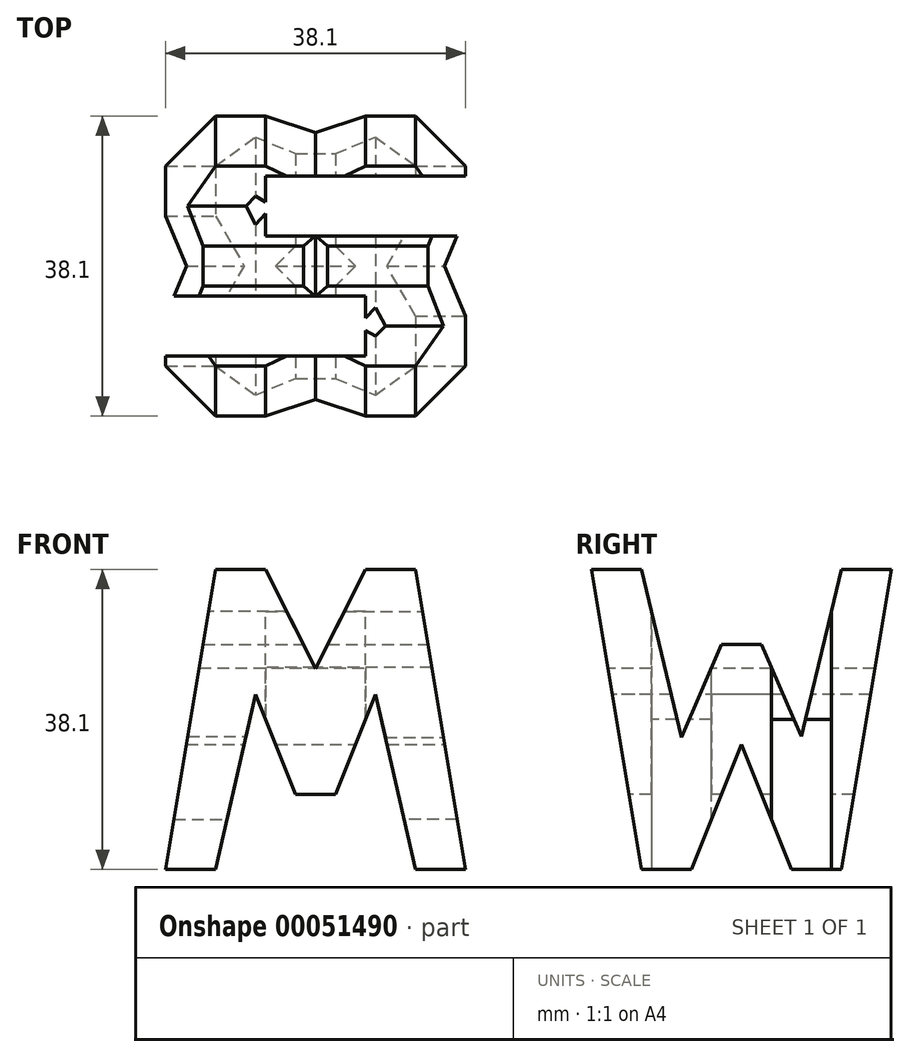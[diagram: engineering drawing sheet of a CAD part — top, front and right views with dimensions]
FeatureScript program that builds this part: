
annotation { "Feature Type Name" : "Feature", "Feature Type Description" : "" }
export const myFeature = defineFeature(function(context is Context, id is Id, definition is map)
    precondition{}
    {
        {
            var Q0;
            Q0=qCreatedBy(makeId("Front.planeOp"),FACE);
            var sketch = newSketch(context, id + "F0", { "sketchPlane" : qUnion([Q0])});
            skLineSegment(sketch, "E0", {"start": v(0, 38.1) * mm, "end": v(0, 0) * mm});
            skLineSegment(sketch, "E1", {"start": v(0, 0) * mm, "end": v(38.1, 0) * mm});
            skLineSegment(sketch, "E2", {"start": v(38.1, 0) * mm, "end": v(38.1, 38.1) * mm});
            skLineSegment(sketch, "E3", {"start": v(38.1, 38.1) * mm, "end": v(0, 38.1) * mm});
            skSolve(sketch);
        }
        {
            var Q0;
            Q0=makeQuery(id+"F0.imprint","IMPRINT",FACE,{"disambiguationData":[TD([[makeQuery(id+"F0.imprint","IMPRINT",EDGE,{"derivedFrom":sQuery(id+"F0.wireOp",EDGE,"E0")}),1.0]])]});
            extrude(context, id + "F1", {"entities" : qUnion([Q0]), "depth" : 38.1 * mm});
        }
        {
            var Q0;
            Q0=qCreatedBy(makeId("Front.planeOp"),FACE);
            cPlane(context, id + "F2", {"entities" : qUnion([Q0]), "cplaneType" : CPlaneType.OFFSET, "offset" : 38.1 * mm, "width" : 152.4 * mm, "height" : 152.4 * mm});
        }
        {
            var Q0;
            Q0=qCreatedBy(makeId("Top.planeOp"),FACE);
            cPlane(context, id + "F3", {"entities" : qUnion([Q0]), "cplaneType" : CPlaneType.OFFSET, "offset" : 38.1 * mm, "width" : 152.4 * mm, "height" : 152.4 * mm});
        }
        {
            var Q0;
            Q0=makeQuery(id+"F1.opExtrude","SWEPT_FACE",FACE,{"disambiguationData":[OSD([sQuery(id+"F0.wireOp",EDGE,"E2")])]});
            var sketch = newSketch(context, id + "F4", { "sketchPlane" : qUnion([Q0])});
            skLineSegment(sketch, "E4", {"start": v(-38.1, 38.1) * mm, "end": v(-31.75, 0) * mm});
            skLineSegment(sketch, "E5", {"start": v(-25.4, 0) * mm, "end": v(-19.05, 15.87) * mm});
            skLineSegment(sketch, "E6", {"start": v(-19.05, 15.87) * mm, "end": v(-12.7, 0) * mm});
            skLineSegment(sketch, "E7", {"start": v(0, 38.1) * mm, "end": v(-6.35, 0) * mm});
            skLineSegment(sketch, "E8", {"start": v(-31.75, 38.1) * mm, "end": v(-26.67, 16.76) * mm});
            skLineSegment(sketch, "E9", {"start": v(-26.67, 16.76) * mm, "end": v(-21.59, 28.57) * mm});
            skLineSegment(sketch, "E10", {"start": v(-21.59, 28.57) * mm, "end": v(-16.5, 28.57) * mm});
            skLineSegment(sketch, "E11", {"start": v(-16.5, 28.57) * mm, "end": v(-11.43, 16.89) * mm});
            skLineSegment(sketch, "E12", {"start": v(-11.43, 16.89) * mm, "end": v(-6.35, 38.1) * mm});
            skSolve(sketch);
        }
        {
            var Q0;
            {var subQ0=sQuery(id+"F4.wireOp",EDGE,"E8");Q0=makeQuery(id+"F4.imprint","IMPRINT",FACE,{"disambiguationData":[TD([[makeQuery(id+"F4.imprint","IMPRINT",EDGE,{"derivedFrom":subQ0}),1.0]])]});}
            var Q1;
            {var subQ0=sQuery(id+"F4.wireOp",EDGE,"E4");Q1=makeQuery(id+"F4.imprint","IMPRINT",FACE,{"disambiguationData":[TD([[makeQuery(id+"F4.imprint","IMPRINT",EDGE,{"derivedFrom":subQ0}),-1.0]])]});}
            var Q2;
            {var subQ0=sQuery(id+"F4.wireOp",EDGE,"E5");Q2=makeQuery(id+"F4.imprint","IMPRINT",FACE,{"disambiguationData":[TD([[makeQuery(id+"F4.imprint","IMPRINT",EDGE,{"derivedFrom":subQ0}),-1.0]])]});}
            var Q3;
            {var subQ0=sQuery(id+"F4.wireOp",EDGE,"E7");Q3=makeQuery(id+"F4.imprint","IMPRINT",FACE,{"disambiguationData":[TD([[makeQuery(id+"F4.imprint","IMPRINT",EDGE,{"derivedFrom":subQ0}),1.0]])]});}
            extrude(context, id + "F5", {"entities" : qUnion([Q0, Q1, Q2, Q3]), "operationType" : NewBodyOperationType.REMOVE, "oppositeDirection" : true, "depth" : 38.1 * mm});
        }
        {
            var Q0;
            Q0=qCreatedBy(id+"F2.planeOp",FACE);
            var sketch = newSketch(context, id + "F6", { "sketchPlane" : qUnion([Q0])});
            skLineSegment(sketch, "E13", {"start": v(0, 0) * mm, "end": v(0, 38.1) * mm});
            skLineSegment(sketch, "E14", {"start": v(0, 38.1) * mm, "end": v(38.1, 38.1) * mm});
            skLineSegment(sketch, "E15", {"start": v(38.1, 38.1) * mm, "end": v(38.1, 0) * mm});
            skLineSegment(sketch, "E16", {"start": v(38.1, 0) * mm, "end": v(0, 0) * mm});
            skLineSegment(sketch, "E17", {"start": v(0, 0) * mm, "end": v(6.35, 38.1) * mm});
            skLineSegment(sketch, "E18", {"start": v(38.1, 0) * mm, "end": v(31.75, 38.1) * mm});
            skLineSegment(sketch, "E19", {"start": v(12.7, 38.1) * mm, "end": v(19.05, 25.51) * mm});
            skLineSegment(sketch, "E20", {"start": v(19.05, 25.51) * mm, "end": v(25.4, 38.1) * mm});
            skLineSegment(sketch, "E21", {"start": v(6.35, 0) * mm, "end": v(11.43, 22.23) * mm});
            skLineSegment(sketch, "E22", {"start": v(11.43, 22.23) * mm, "end": v(16.51, 9.52) * mm});
            skLineSegment(sketch, "E23", {"start": v(16.51, 9.53) * mm, "end": v(21.59, 9.52) * mm});
            skLineSegment(sketch, "E24", {"start": v(21.59, 9.52) * mm, "end": v(26.67, 22.23) * mm});
            skLineSegment(sketch, "E25", {"start": v(26.67, 22.23) * mm, "end": v(31.75, 0) * mm});
            skSolve(sketch);
        }
        {
            var Q0;
            {var subQ0=sQuery(id+"F6.wireOp",EDGE,"E13");Q0=makeQuery(id+"F6.imprint","IMPRINT",FACE,{"disambiguationData":[TD([[makeQuery(id+"F6.imprint","IMPRINT",EDGE,{"derivedFrom":subQ0}),-1.0]])]});}
            var Q1;
            {var subQ0=sQuery(id+"F6.wireOp",EDGE,"E19");Q1=makeQuery(id+"F6.imprint","IMPRINT",FACE,{"disambiguationData":[TD([[makeQuery(id+"F6.imprint","IMPRINT",EDGE,{"derivedFrom":subQ0}),1.0]])]});}
            var Q2;
            {var subQ1=sQuery(id+"F6.wireOp",EDGE,"E21");Q2=makeQuery(id+"F6.imprint","IMPRINT",FACE,{"disambiguationData":[TD([[makeQuery(id+"F6.imprint","IMPRINT",EDGE,{"derivedFrom":subQ1}),-1.0]])]});}
            var Q3;
            {var subQ0=sQuery(id+"F6.wireOp",EDGE,"E15");Q3=makeQuery(id+"F6.imprint","IMPRINT",FACE,{"disambiguationData":[TD([[makeQuery(id+"F6.imprint","IMPRINT",EDGE,{"derivedFrom":subQ0}),-1.0]])]});}
            extrude(context, id + "F7", {"entities" : qUnion([Q0, Q1, Q2, Q3]), "operationType" : NewBodyOperationType.REMOVE, "oppositeDirection" : true, "depth" : 38.1 * mm});
        }
        {
            var Q0;
            Q0=qCreatedBy(id+"F3.planeOp",FACE);
            var sketch = newSketch(context, id + "F8", { "sketchPlane" : qUnion([Q0])});
            skLineSegment(sketch, "E26", {"start": v(38.1, 0) * mm, "end": v(38.1, -38.1) * mm});
            skLineSegment(sketch, "E27", {"start": v(38.1, -38.1) * mm, "end": v(0, -38.1) * mm});
            skLineSegment(sketch, "E28", {"start": v(0, -38.1) * mm, "end": v(0, 0) * mm});
            skLineSegment(sketch, "E29", {"start": v(0, 0) * mm, "end": v(38.1, 0) * mm});
            skLineSegment(sketch, "E30", {"start": v(38.1, -7.62) * mm, "end": v(12.7, -7.62) * mm});
            skLineSegment(sketch, "E31", {"start": v(12.7, -7.62) * mm, "end": v(12.7, -15.24) * mm});
            skLineSegment(sketch, "E32", {"start": v(12.7, -15.24) * mm, "end": v(38.1, -15.24) * mm});
            skLineSegment(sketch, "E33", {"start": v(0, -30.48) * mm, "end": v(25.4, -30.48) * mm});
            skLineSegment(sketch, "E34", {"start": v(25.4, -30.48) * mm, "end": v(25.4, -22.86) * mm});
            skLineSegment(sketch, "E35", {"start": v(25.4, -22.86) * mm, "end": v(0, -22.86) * mm});
            skSolve(sketch);
        }
        {
            var Q0;
            {var subQ0=sQuery(id+"F8.wireOp",EDGE,"E30");Q0=makeQuery(id+"F8.imprint","IMPRINT",FACE,{"disambiguationData":[TD([[makeQuery(id+"F8.imprint","IMPRINT",EDGE,{"derivedFrom":subQ0}),1.0]])]});}
            var Q1;
            {var subQ0=sQuery(id+"F8.wireOp",EDGE,"E33");Q1=makeQuery(id+"F8.imprint","IMPRINT",FACE,{"disambiguationData":[TD([[makeQuery(id+"F8.imprint","IMPRINT",EDGE,{"derivedFrom":subQ0}),1.0]])]});}
            extrude(context, id + "F9", {"entities" : qUnion([Q0, Q1]), "operationType" : NewBodyOperationType.REMOVE, "oppositeDirection" : true, "depth" : 38.1 * mm});
        }
    });
